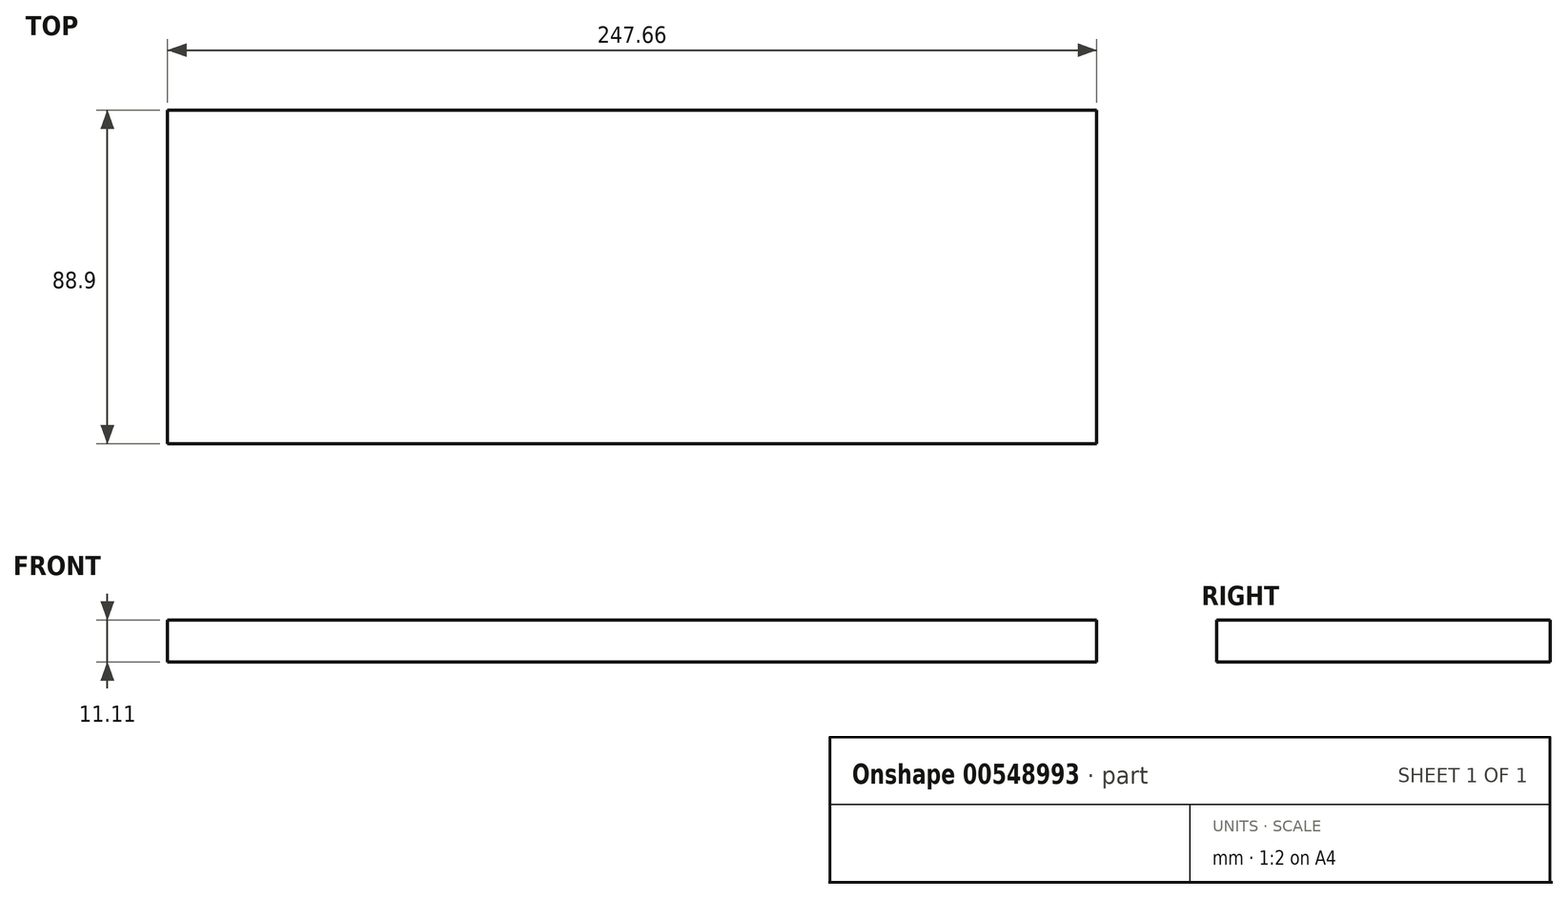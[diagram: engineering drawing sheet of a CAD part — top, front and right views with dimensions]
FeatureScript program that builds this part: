
annotation { "Feature Type Name" : "Feature", "Feature Type Description" : "" }
export const myFeature = defineFeature(function(context is Context, id is Id, definition is map)
    precondition{}
    {
        {
            var Q0;
            Q0=qCreatedBy(makeId("Top.planeOp"),FACE);
            var sketch = newSketch(context, id + "F0", { "sketchPlane" : qUnion([Q0])});
            skLineSegment(sketch, "E0.bottom", {"start": v(123.83, -44.45) * mm, "end": v(-123.83, -44.45) * mm});
            skLineSegment(sketch, "E0.top", {"start": v(123.83, 44.45) * mm, "end": v(-123.83, 44.45) * mm});
            skLineSegment(sketch, "E0.left", {"start": v(123.83, -44.45) * mm, "end": v(123.83, 44.45) * mm});
            skLineSegment(sketch, "E0.right", {"start": v(-123.83, -44.45) * mm, "end": v(-123.83, 44.45) * mm});
            skPoint(sketch, "E0.middle", {"position": v(0, 0) * mm});
            skSolve(sketch);
        }
        {
            var Q0;
            Q0 = qSketchRegion(id + "F0", true);
            extrude(context, id + "F1", {"entities" : qUnion([Q0]), "depth" : 11.1 * mm, "offsetDistance" : 25.4 * mm});
        }
    });
